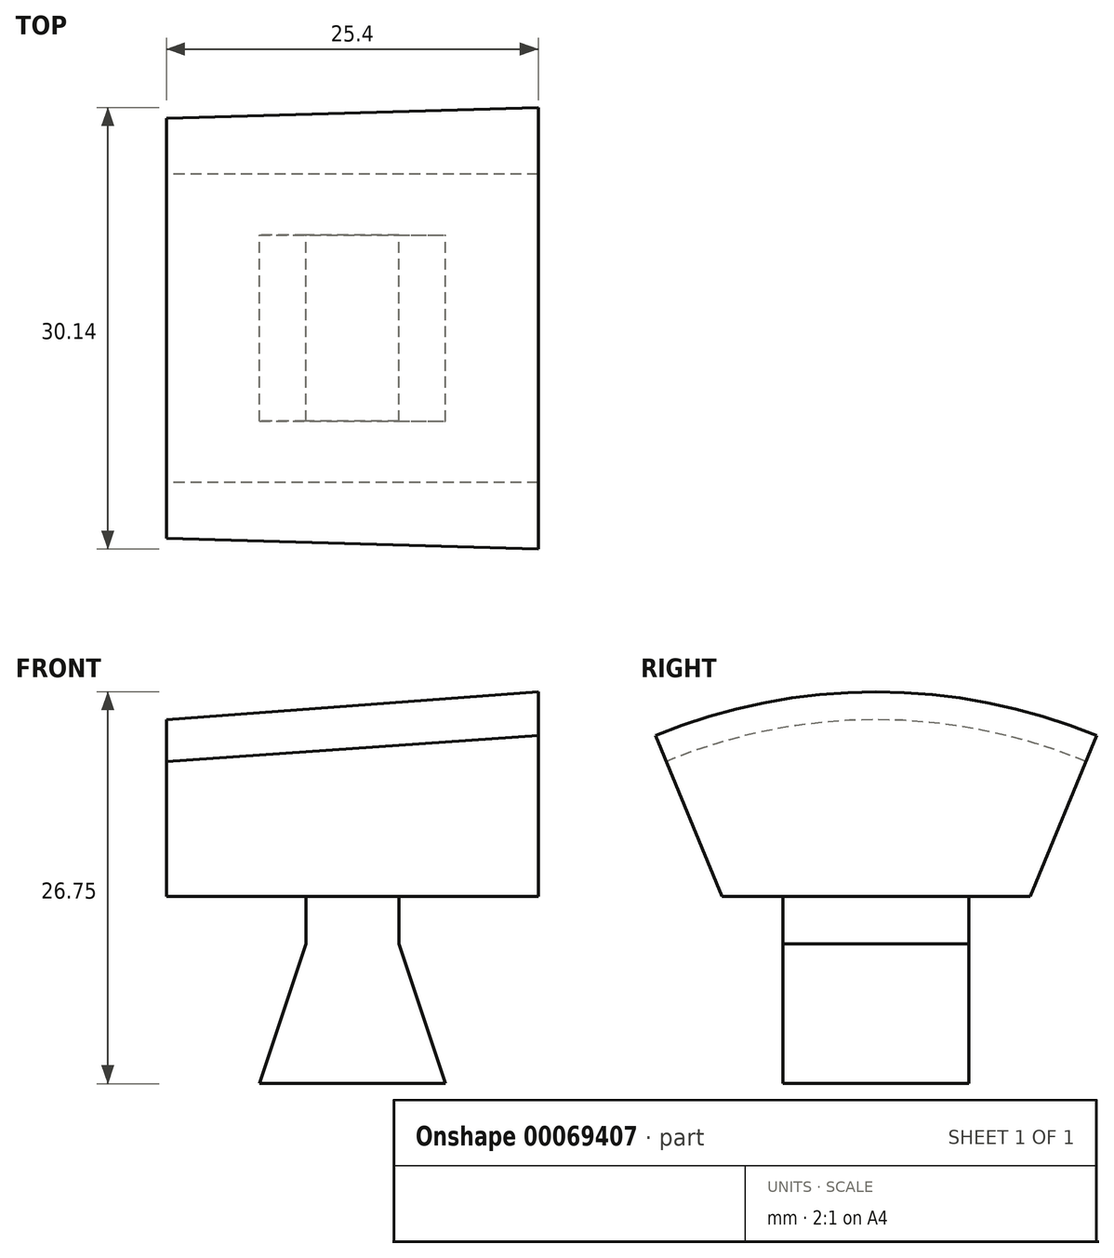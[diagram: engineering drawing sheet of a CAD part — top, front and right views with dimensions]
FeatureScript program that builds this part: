
annotation { "Feature Type Name" : "Feature", "Feature Type Description" : "" }
export const myFeature = defineFeature(function(context is Context, id is Id, definition is map)
    precondition{}
    {
        {
            var Q0;
            Q0=qCreatedBy(makeId("Front.planeOp"),FACE);
            var sketch = newSketch(context, id + "F0", { "sketchPlane" : qUnion([Q0])});
            skLineSegment(sketch, "E0", {"start": v(0, 0) * mm, "end": v(-61.12, 0) * mm});
            skLineSegment(sketch, "E1.bottom", {"start": v(0, 25.4) * mm, "end": v(-9.53, 25.4) * mm});
            skLineSegment(sketch, "E1.left", {"start": v(0, 25.4) * mm, "end": v(0, 39.37) * mm});
            skLineSegment(sketch, "E1.right", {"start": v(-25.4, 25.4) * mm, "end": v(-25.4, 37.47) * mm});
            skLineSegment(sketch, "E2", {"start": v(0, 39.37) * mm, "end": v(-25.4, 37.47) * mm});
            skPoint(sketch, "E3.orphan", {"position": v(-25.4, 39.37) * mm});
            skLineSegment(sketch, "E4.left", {"start": v(-15.88, 25.4) * mm, "end": v(-15.88, 22.15) * mm});
            skLineSegment(sketch, "E4.right", {"start": v(-9.53, 25.4) * mm, "end": v(-9.53, 22.15) * mm});
            skLineSegment(sketch, "E5.top", {"start": v(-19.05, 12.62) * mm, "end": v(-6.35, 12.62) * mm});
            skLineSegment(sketch, "E6", {"start": v(-15.88, 22.15) * mm, "end": v(-19.05, 12.62) * mm});
            skLineSegment(sketch, "E7", {"start": v(-9.53, 22.15) * mm, "end": v(-6.35, 12.62) * mm});
            skPoint(sketch, "E8.orphan", {"position": v(-19.05, 22.15) * mm});
            skLineSegment(sketch, "E9.trimOffspring", {"start": v(-15.88, 25.4) * mm, "end": v(-25.4, 25.4) * mm});
            skLineSegment(sketch, "E10", {"start": v(-15.88, 25.4) * mm, "end": v(-9.53, 25.4) * mm});
            skLineSegment(sketch, "E11", {"start": v(16.79, 25.4) * mm, "end": v(-48.48, 25.4) * mm});
            skSolve(sketch);
        }
        {
            var Q0;
            Q0=makeQuery(id+"F0.imprint","IMPRINT",FACE,{"disambiguationData":[TD([[makeQuery(id+"F0.imprint","IMPRINT",EDGE,{"derivedFrom":sQuery(id+"F0.wireOp",EDGE,"E4.left")}),1.0]])]});
            extrude(context, id + "F1", {"entities" : qUnion([Q0]), "endBound" : BoundingType.SYMMETRIC, "depth" : 12.7 * mm});
        }
        {
            var Q0;
            {var subQ1=sQuery(id+"F0.wireOp",EDGE,"E1.left");Q0=makeQuery(id+"F0.imprint","IMPRINT",FACE,{"disambiguationData":[TD([[makeQuery(id+"F0.imprint","IMPRINT",EDGE,{"derivedFrom":subQ1}),1.0]])]});}
            var Q1;
            Q1=sQuery(id+"F0.wireOp",EDGE,"E0");
            revolve(context, id + "F2", {"operationType" : NewBodyOperationType.ADD, "entities" : qUnion([Q0]), "axis" : qUnion([Q1]), "revolveType" : RevolveType.SYMMETRIC, "angle" : 45 * degree});
        }
        {
            var Q0;
            Q0=makeQuery(id+"F2.opRevolve","SWEPT_FACE",FACE,{"disambiguationData":[OSD([sQuery(id+"F0.wireOp",EDGE,"E1.left")])]});
            var sketch = newSketch(context, id + "F3", { "sketchPlane" : qUnion([Q0])});
            skArc(sketch, "E12.0.0", {"start": v(15.07, 36.37) * mm, "mid": v(0, 39.37) * mm, "end": v(-15.07, 36.37) * mm});
            skLineSegment(sketch, "E12.0.1", {"start": v(-15.07, 36.37) * mm, "end": v(-9.72, 23.47) * mm});
            skArc(sketch, "E12.0.2", {"start": v(-9.72, 23.47) * mm, "mid": v(0, 25.4) * mm, "end": v(9.72, 23.47) * mm});
            skLineSegment(sketch, "E12.0.3", {"start": v(9.72, 23.47) * mm, "end": v(15.07, 36.37) * mm});
            skLineSegment(sketch, "E13.0", {"start": v(0, 25.4) * mm, "end": v(0, 39.37) * mm});
            skLineSegment(sketch, "E14.bottom", {"start": v(0, 25.4) * mm, "end": v(-11.5, 25.4) * mm});
            skLineSegment(sketch, "E14.top", {"start": v(0, 22.86) * mm, "end": v(-11.5, 22.86) * mm});
            skLineSegment(sketch, "E14.left", {"start": v(0, 25.4) * mm, "end": v(0, 22.86) * mm});
            skLineSegment(sketch, "E14.right", {"start": v(-11.5, 25.4) * mm, "end": v(-11.5, 22.86) * mm});
            skLineSegment(sketch, "E15.bottom", {"start": v(0, 25.4) * mm, "end": v(11.38, 25.4) * mm});
            skLineSegment(sketch, "E15.top", {"start": v(0, 22.86) * mm, "end": v(11.38, 22.86) * mm});
            skLineSegment(sketch, "E15.right", {"start": v(11.38, 25.4) * mm, "end": v(11.38, 22.86) * mm});
            skSolve(sketch);
        }
        {
            var Q0;
            Q0=makeQuery(id+"F3.imprint","IMPRINT",FACE,{"disambiguationData":[TD([[makeQuery(id+"F3.imprint","IMPRINT",EDGE,{"derivedFrom":sQuery(id+"F3.wireOp",EDGE,"E14.top")}),-1.0]])]});
            var Q1;
            Q1=makeQuery(id+"F3.imprint","IMPRINT",FACE,{"disambiguationData":[TD([[makeQuery(id+"F3.imprint","IMPRINT",EDGE,{"derivedFrom":sQuery(id+"F3.wireOp",EDGE,"E15.top")}),1.0]])]});
            var Q2;
            {var subQ0=sQuery(id+"F3.wireOp",EDGE,"E12.0.3");var subQ1=sQuery(id+"F3.wireOp",EDGE,"E12.0.2");var subQ2=makeQuery(id+"F3.imprint","INTERSECT",VERTEX,{"derivedFrom":[subQ1,subQ0]});Q2=makeQuery(id+"F3.imprint","IMPRINT",FACE,{"disambiguationData":[TD([[makeQuery(id+"F3.imprint","IMPRINT",EDGE,{"disambiguationData":[TD([[subQ2,-1.0]])],"derivedFrom":subQ0}),1.0]])]});}
            var Q3;
            {var subQ0=sQuery(id+"F3.wireOp",EDGE,"E12.0.2");var subQ1=sQuery(id+"F3.wireOp",EDGE,"E12.0.1");var subQ2=makeQuery(id+"F3.imprint","INTERSECT",VERTEX,{"derivedFrom":[subQ1,subQ0]});Q3=makeQuery(id+"F3.imprint","IMPRINT",FACE,{"disambiguationData":[TD([[makeQuery(id+"F3.imprint","IMPRINT",EDGE,{"disambiguationData":[TD([[subQ2,-1.0]])],"derivedFrom":subQ1}),-1.0]])]});}
            extrude(context, id + "F4", {"entities" : qUnion([Q0, Q1, Q2, Q3]), "operationType" : NewBodyOperationType.REMOVE, "endBound" : BoundingType.THROUGH_ALL, "oppositeDirection" : true, "depth" : 25.4 * mm});
        }
        {
            var Q0;
            Q0=makeQuery(id+"F4.boolean.opBoolean","COPY",FACE,{"derivedFrom":makeQuery(id+"F4.opExtrude","SWEPT_FACE",FACE,{"disambiguationData":[OSD([sQuery(id+"F3.wireOp",EDGE,"E14.top"),sQuery(id+"F3.wireOp",EDGE,"E15.top")])]})});
            extrude(context, id + "F5", {"entities" : qUnion([Q0]), "operationType" : NewBodyOperationType.ADD, "endBound" : BoundingType.UP_TO_NEXT, "depth" : 25.4 * mm});
        }
    });
